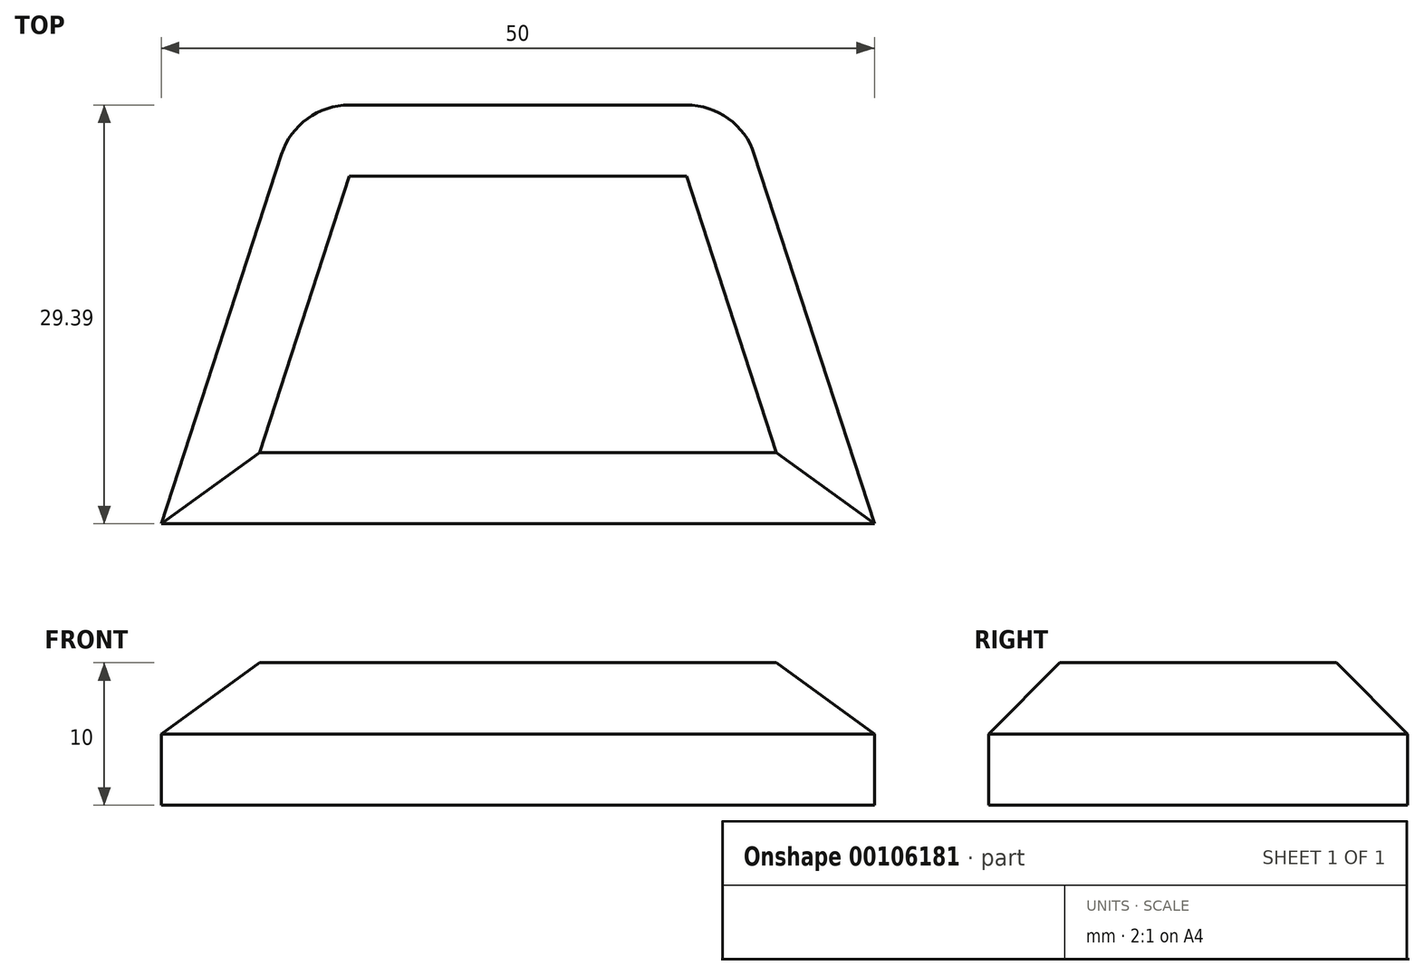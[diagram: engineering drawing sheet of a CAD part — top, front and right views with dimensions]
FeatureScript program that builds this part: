
annotation { "Feature Type Name" : "Feature", "Feature Type Description" : "" }
export const myFeature = defineFeature(function(context is Context, id is Id, definition is map)
    precondition{}
    {
        {
            var Q0;
            Q0=qCreatedBy(makeId("Top.planeOp"),FACE);
            var sketch = newSketch(context, id + "F0", { "sketchPlane" : qUnion([Q0])});
            skArc(sketch, "E0.cCircle", {"start": v(19.65, -8.12) * mm, "mid": v(0, 21.27) * mm, "end": v(-19.65, -8.12) * mm, "construction": true});
            skLineSegment(sketch, "E0.2", {"start": v(-25, -8.12) * mm, "end": v(-15.45, 21.27) * mm});
            skLineSegment(sketch, "E0.3", {"start": v(-15.45, 21.27) * mm, "end": v(15.45, 21.27) * mm});
            skLineSegment(sketch, "E0.4", {"start": v(15.45, 21.27) * mm, "end": v(25, -8.12) * mm});
            skLineSegment(sketch, "E1", {"start": v(-25, -8.12) * mm, "end": v(25, -8.12) * mm});
            skSolve(sketch);
        }
        {
            var Q0;
            Q0 = qSketchRegion(id + "F0", true);
            extrude(context, id + "F1", {"entities" : qUnion([Q0]), "depth" : 10 * mm});
        }
        {
            var Q0;
            Q0=makeQuery(id+"F1.opExtrude","SWEPT_EDGE",EDGE,{"disambiguationData":[OSD([sQuery(id+"F0.wireOp",EDGE,"E0.3"),sQuery(id+"F0.wireOp",EDGE,"E0.4")])]});
            fillet(context, id + "F2", {"entities" : qUnion([Q0]), "radius" : 5 * mm, "tangentPropagation" : true, "allowEdgeOverflow" : false});
        }
        {
            var Q0;
            Q0=makeQuery(id+"F1.opExtrude","SWEPT_EDGE",EDGE,{"disambiguationData":[OSD([sQuery(id+"F0.wireOp",EDGE,"E0.2"),sQuery(id+"F0.wireOp",EDGE,"E0.3")])]});
            fillet(context, id + "F3", {"entities" : qUnion([Q0]), "radius" : 5 * mm, "tangentPropagation" : true, "allowEdgeOverflow" : false});
        }
        {
            var Q0;
            Q0=makeQuery(id+"F1.opExtrude","CAP_FACE",FACE,{"disambiguationData":[OSD([sQuery(id+"F0.wireOp",EDGE,"E0.2"),sQuery(id+"F0.wireOp",EDGE,"E0.3"),sQuery(id+"F0.wireOp",EDGE,"E0.4"),sQuery(id+"F0.wireOp",EDGE,"E1")])],"isStart":false});
            chamfer(context, id + "F4", {"entities" : qUnion([Q0]), "width" : 5 * mm, "tangentPropagation" : true});
        }
    });
